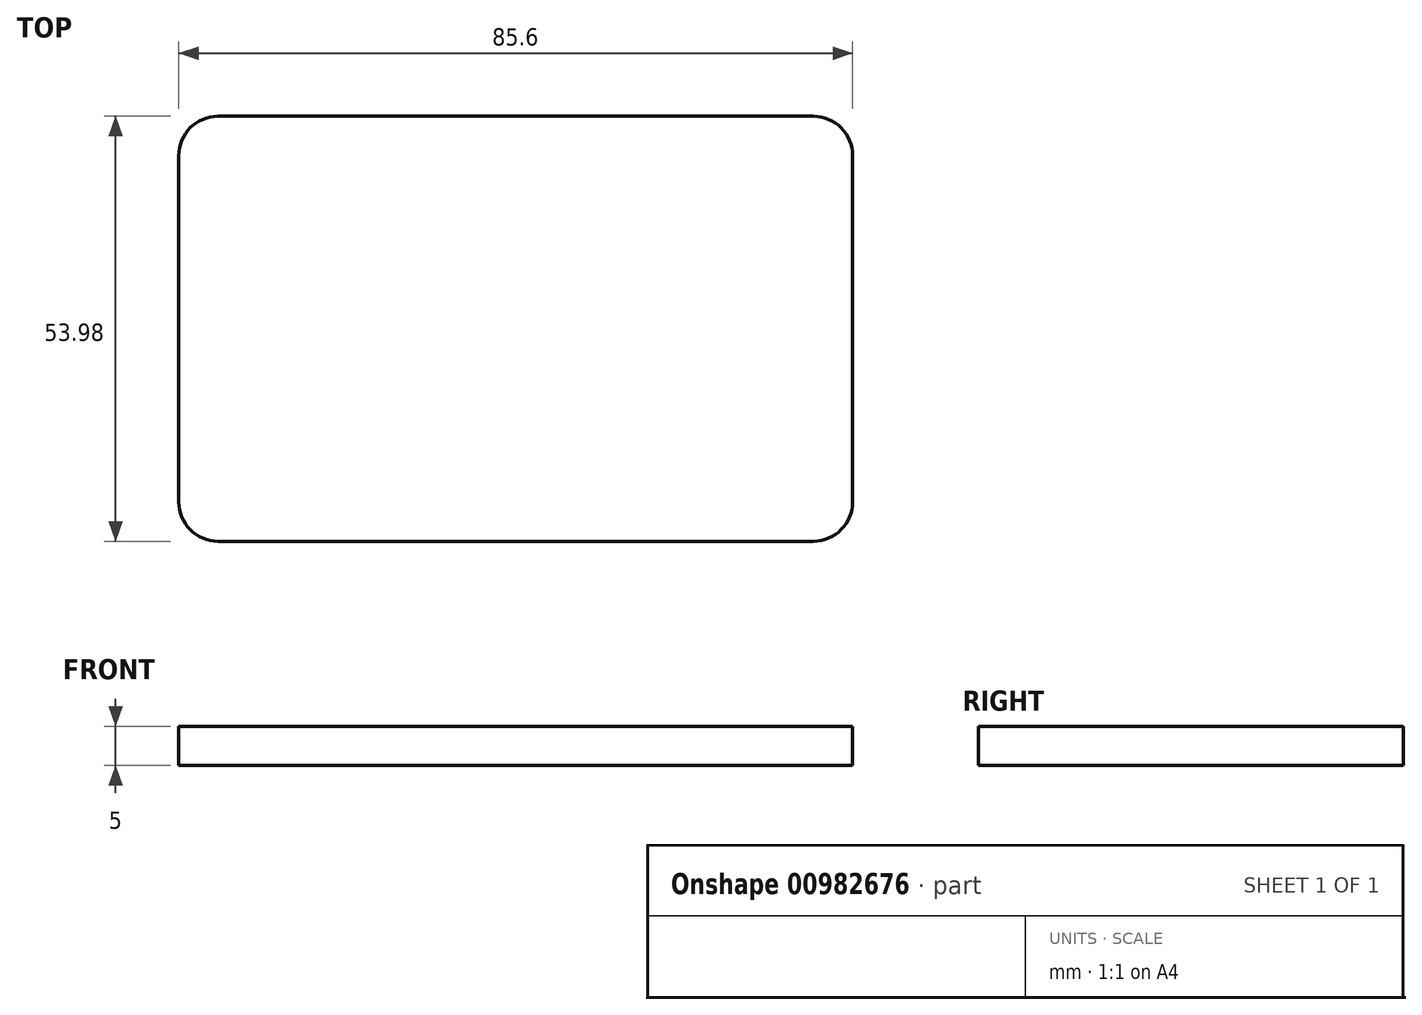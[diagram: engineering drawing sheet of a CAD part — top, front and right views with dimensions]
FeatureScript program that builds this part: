
annotation { "Feature Type Name" : "Feature", "Feature Type Description" : "" }
export const myFeature = defineFeature(function(context is Context, id is Id, definition is map)
    precondition{}
    {
        {
            var Q0;
            Q0=qCreatedBy(makeId("Top.planeOp"),FACE);
            var sketch = newSketch(context, id + "F0", { "sketchPlane" : qUnion([Q0])});
            skLineSegment(sketch, "E0.bottom", {"start": v(0, 0) * mm, "end": v(85.6, 0) * mm});
            skLineSegment(sketch, "E0.top", {"start": v(0, 53.98) * mm, "end": v(85.6, 53.98) * mm});
            skLineSegment(sketch, "E0.left", {"start": v(0, 0) * mm, "end": v(0, 53.98) * mm});
            skLineSegment(sketch, "E0.right", {"start": v(85.6, 0) * mm, "end": v(85.6, 53.98) * mm});
            skSolve(sketch);
        }
        {
            var Q0;
            Q0=makeQuery(id+"F0.imprint","IMPRINT",FACE,{"disambiguationData":[TD([[makeQuery(id+"F0.imprint","IMPRINT",EDGE,{"derivedFrom":sQuery(id+"F0.wireOp",EDGE,"E0.bottom")}),1.0]])]});
            extrude(context, id + "F1", {"entities" : qUnion([Q0]), "depth" : 5 * mm, "offsetDistance" : 25 * mm});
        }
        {
            var Q0;
            Q0=makeQuery(id+"F1.opExtrude","SWEPT_EDGE",EDGE,{"disambiguationData":[OSD([sQuery(id+"F0.wireOp",EDGE,"E0.bottom"),sQuery(id+"F0.wireOp",EDGE,"E0.right")])]});
            var Q1;
            Q1=makeQuery(id+"F1.opExtrude","SWEPT_EDGE",EDGE,{"disambiguationData":[OSD([sQuery(id+"F0.wireOp",EDGE,"E0.top"),sQuery(id+"F0.wireOp",EDGE,"E0.right")])]});
            var Q2;
            Q2=makeQuery(id+"F1.opExtrude","SWEPT_EDGE",EDGE,{"disambiguationData":[OSD([sQuery(id+"F0.wireOp",EDGE,"E0.bottom"),sQuery(id+"F0.wireOp",EDGE,"E0.left")])]});
            var Q3;
            Q3=makeQuery(id+"F1.opExtrude","SWEPT_EDGE",EDGE,{"disambiguationData":[OSD([sQuery(id+"F0.wireOp",EDGE,"E0.top"),sQuery(id+"F0.wireOp",EDGE,"E0.left")])]});
            fillet(context, id + "F2", {"entities" : qUnion([Q0, Q1, Q2, Q3]), "radius" : 5 * mm, "tangentPropagation" : true, "allowEdgeOverflow" : false});
        }
    });
